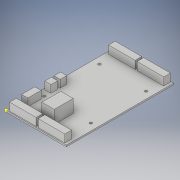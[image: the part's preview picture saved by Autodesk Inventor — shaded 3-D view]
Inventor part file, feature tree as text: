
AUTODESK INVENTOR PART (.ipt)
format: ipt  version: 2018 (Build 220112000, 112)  size: 175,616 bytes
history: native  units: mm
features: sketch x5, extrude x4
ambient origin geometry x8: Origin, YZ Plane, XZ Plane, XY Plane, X Axis, Y Axis, Z Axis, Center Point
bodies: Solid1 (feature_tree)
feature tree (9):
  extrude  "Extrusion1"  Depth=113.0mm
  sketch  "Sketch2"  dims[d2=49.0mm d3=58.0mm]
  extrude  "Extrusion2"  Depth=58.0mm
  extrude  "Extrusion3"  Depth=22.0mm
  extrude  "Extrusion4"  Depth=28.0mm
  sketch  "Sketch1"  dims[d0=63.23mm d1=113.0mm]
  sketch  "Sketch3"  dims[d4=2.7mm d5=22.0mm]
  sketch  "Sketch4"  dims[d6=1.6mm d7=0.0mm d8=28.0mm]
  sketch  "Sketch5"  dims[d9=2.0mm d10=2.0mm d11=7.0mm d12=1.0mm d13=1.0mm d14=63.23mm d15=2.615mm d16=2.615mm d17=8.3mm d18=0.0mm d19=6.5mm d20=14.0mm d21=28.5mm d22=1.6mm d23=8.0mm d24=0.0mm d25=12.3mm d26=13.0mm d27=20.0mm d28=13.8mm d29=0.0mm d30=7.0mm d31=7.0mm d32=10.5mm d33=2.5mm]
